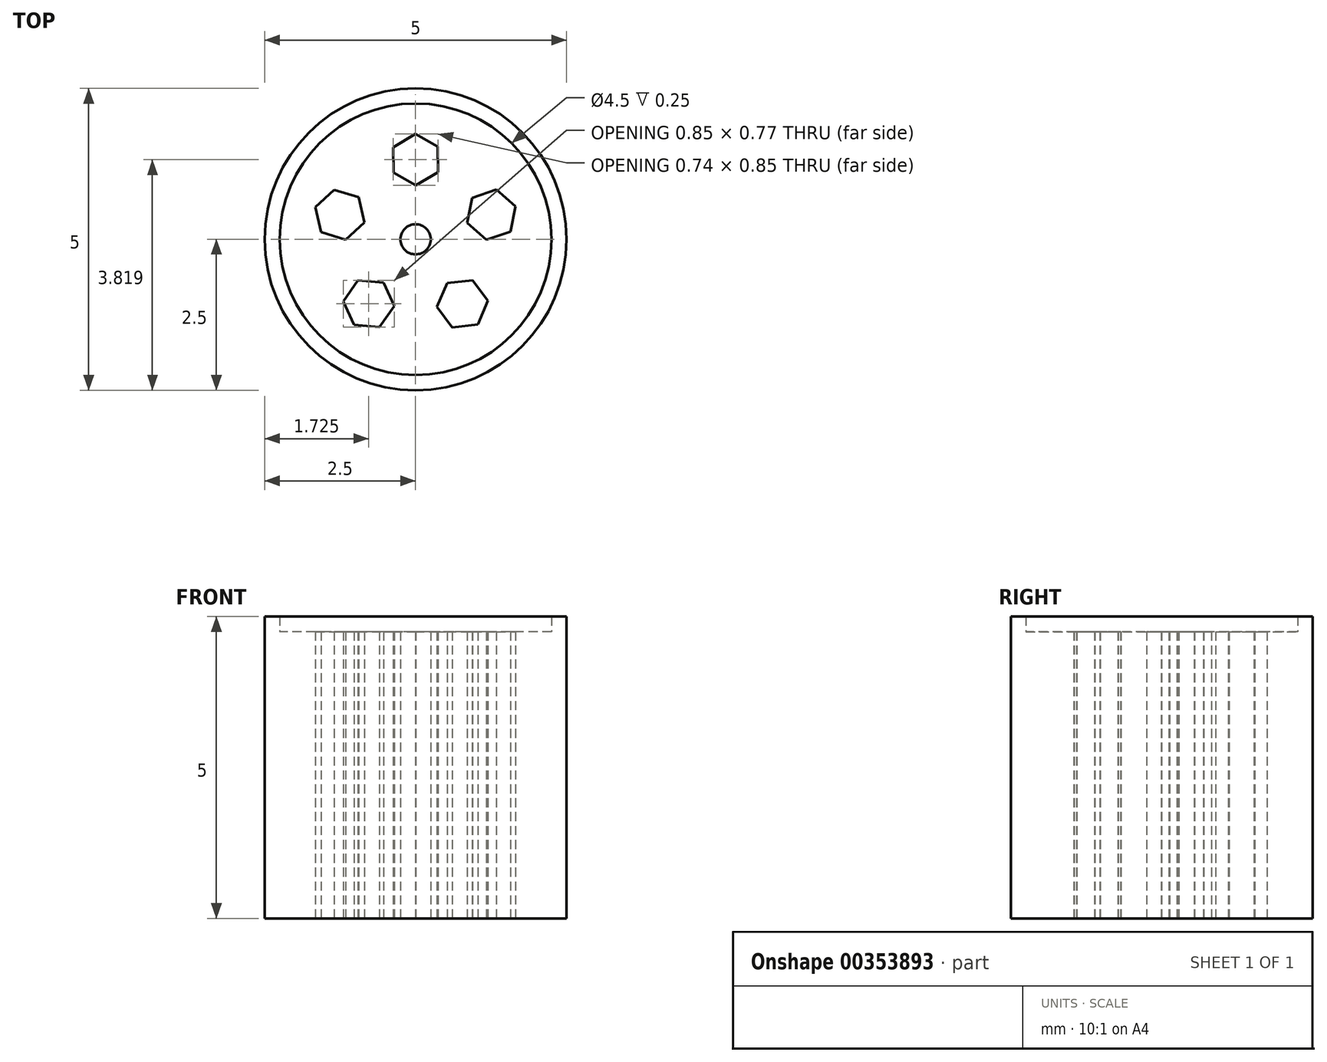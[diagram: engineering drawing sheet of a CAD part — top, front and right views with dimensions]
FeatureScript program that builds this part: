
annotation { "Feature Type Name" : "Feature", "Feature Type Description" : "" }
export const myFeature = defineFeature(function(context is Context, id is Id, definition is map)
    precondition{}
    {
        {
            var Q0;
            Q0=qCreatedBy(makeId("Top.planeOp"),FACE);
            var sketch = newSketch(context, id + "F0", { "sketchPlane" : qUnion([Q0])});
            skCircle(sketch, "E0", {"center": v(0, 0) * mm, "radius": 2.5 * mm});
            skCircle(sketch, "E1", {"center": v(0, 0) * mm, "radius": 0.25 * mm});
            skLineSegment(sketch, "E2.0", {"start": v(0, 0.9) * mm, "end": v(-0.36, 1.1) * mm});
            skLineSegment(sketch, "E2.1", {"start": v(-0.36, 1.1) * mm, "end": v(-0.37, 1.53) * mm});
            skLineSegment(sketch, "E2.2", {"start": v(-0.37, 1.53) * mm, "end": v(0, 1.74) * mm});
            skLineSegment(sketch, "E2.3", {"start": v(0, 1.74) * mm, "end": v(0.36, 1.54) * mm});
            skLineSegment(sketch, "E2.4", {"start": v(0.36, 1.54) * mm, "end": v(0.37, 1.11) * mm});
            skLineSegment(sketch, "E2.5", {"start": v(0.37, 1.11) * mm, "end": v(0, 0.9) * mm});
            skPoint(sketch, "E2.0.midPoint", {"position": v(-0.18, 1) * mm});
            skPoint(sketch, "E3.1.0", {"position": v(-1, 0.14) * mm});
            skLineSegment(sketch, "E3.1.1", {"start": v(-0.94, 0.7) * mm, "end": v(-0.85, 0.28) * mm});
            skLineSegment(sketch, "E3.1.2", {"start": v(-1.35, 0.82) * mm, "end": v(-0.94, 0.7) * mm});
            skLineSegment(sketch, "E3.1.3", {"start": v(-1.66, 0.53) * mm, "end": v(-1.35, 0.82) * mm});
            skLineSegment(sketch, "E3.1.4", {"start": v(-1.57, 0.12) * mm, "end": v(-1.66, 0.53) * mm});
            skLineSegment(sketch, "E3.1.5", {"start": v(-1.16, 0) * mm, "end": v(-1.57, 0.12) * mm});
            skLineSegment(sketch, "E3.1.6", {"start": v(-0.85, 0.28) * mm, "end": v(-1.16, 0) * mm});
            skPoint(sketch, "E3.2.0", {"position": v(-0.44, -0.91) * mm});
            skLineSegment(sketch, "E3.2.1", {"start": v(-0.95, -0.68) * mm, "end": v(-0.53, -0.72) * mm});
            skLineSegment(sketch, "E3.2.2", {"start": v(-1.2, -1.03) * mm, "end": v(-0.95, -0.68) * mm});
            skLineSegment(sketch, "E3.2.3", {"start": v(-1.02, -1.41) * mm, "end": v(-1.2, -1.03) * mm});
            skLineSegment(sketch, "E3.2.4", {"start": v(-0.6, -1.45) * mm, "end": v(-1.02, -1.41) * mm});
            skLineSegment(sketch, "E3.2.5", {"start": v(-0.35, -1.1) * mm, "end": v(-0.6, -1.45) * mm});
            skLineSegment(sketch, "E3.2.6", {"start": v(-0.53, -0.72) * mm, "end": v(-0.35, -1.1) * mm});
            skPoint(sketch, "E3.3.0", {"position": v(0.73, -0.7) * mm});
            skLineSegment(sketch, "E3.3.1", {"start": v(0.35, -1.12) * mm, "end": v(0.52, -0.73) * mm});
            skLineSegment(sketch, "E3.3.2", {"start": v(0.6, -1.46) * mm, "end": v(0.35, -1.12) * mm});
            skLineSegment(sketch, "E3.3.3", {"start": v(1.03, -1.4) * mm, "end": v(0.6, -1.46) * mm});
            skLineSegment(sketch, "E3.3.4", {"start": v(1.2, -1.02) * mm, "end": v(1.03, -1.4) * mm});
            skLineSegment(sketch, "E3.3.5", {"start": v(0.94, -0.68) * mm, "end": v(1.2, -1.02) * mm});
            skLineSegment(sketch, "E3.3.6", {"start": v(0.52, -0.73) * mm, "end": v(0.94, -0.68) * mm});
            skPoint(sketch, "E3.4.0", {"position": v(0.9, 0.48) * mm});
            skLineSegment(sketch, "E3.4.1", {"start": v(1.17, 0) * mm, "end": v(0.85, 0.27) * mm});
            skLineSegment(sketch, "E3.4.2", {"start": v(1.57, 0.13) * mm, "end": v(1.17, 0) * mm});
            skLineSegment(sketch, "E3.4.3", {"start": v(1.66, 0.54) * mm, "end": v(1.57, 0.13) * mm});
            skLineSegment(sketch, "E3.4.4", {"start": v(1.34, 0.82) * mm, "end": v(1.66, 0.54) * mm});
            skLineSegment(sketch, "E3.4.5", {"start": v(0.94, 0.69) * mm, "end": v(1.34, 0.82) * mm});
            skLineSegment(sketch, "E3.4.6", {"start": v(0.85, 0.27) * mm, "end": v(0.94, 0.69) * mm});
            skCircle(sketch, "E4", {"center": v(0, 0) * mm, "radius": 2.25 * mm});
            skSolve(sketch);
        }
        {
            var Q0;
            Q0 = qSketchRegion(id + "F0", true);
            extrude(context, id + "F1", {"entities" : qUnion([Q0]), "depth" : 5 * mm});
        }
        {
            var Q0;
            Q0=makeQuery(id+"F0.imprint","IMPRINT",FACE,{"disambiguationData":[TD([[makeQuery(id+"F0.imprint","IMPRINT",EDGE,{"derivedFrom":sQuery(id+"F0.wireOp",EDGE,"E1")}),-1.0]])]});
            extrude(context, id + "F2", {"entities" : qUnion([Q0]), "operationType" : NewBodyOperationType.ADD, "depth" : 4.75 * mm});
        }
    });
